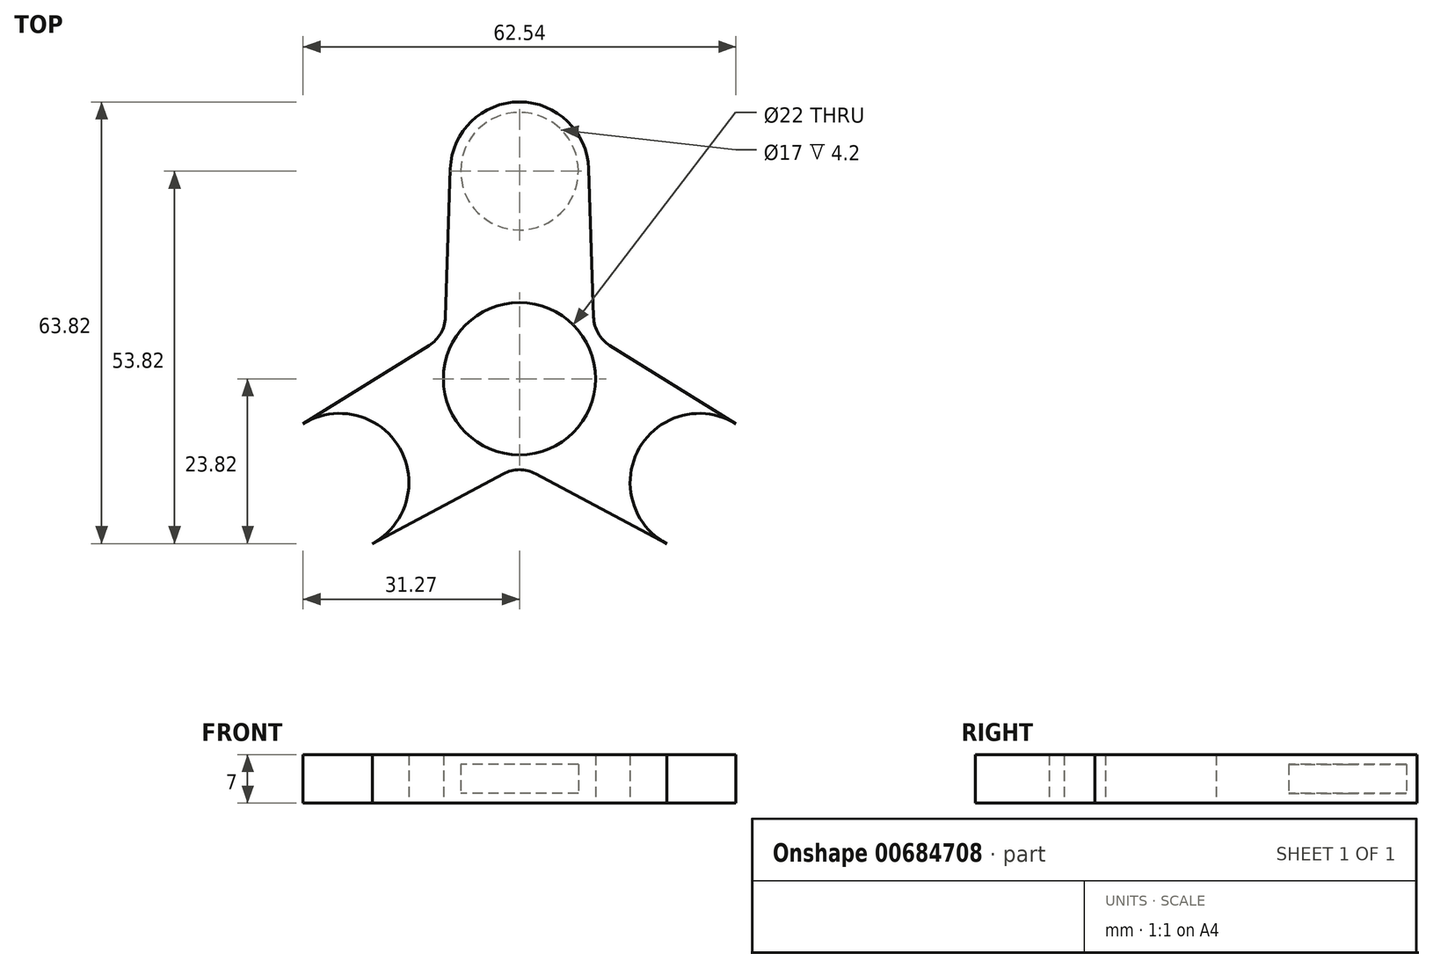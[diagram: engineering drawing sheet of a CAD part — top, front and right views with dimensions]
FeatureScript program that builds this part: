
annotation { "Feature Type Name" : "Feature", "Feature Type Description" : "" }
export const myFeature = defineFeature(function(context is Context, id is Id, definition is map)
    precondition{}
    {
        {
            var Q0;
            Q0=qCreatedBy(makeId("Top.planeOp"),FACE);
            var sketch = newSketch(context, id + "F0", { "sketchPlane" : qUnion([Q0])});
            skCircle(sketch, "E0", {"center": v(0, 0) * mm, "radius": 11 * mm});
            skLineSegment(sketch, "E1", {"start": v(-51.96, 30) * mm, "end": v(51.96, -30) * mm, "construction": true});
            skLineSegment(sketch, "E2.MirrorCS", {"start": v(51.96, 30) * mm, "end": v(-51.96, -30) * mm, "construction": true});
            skCircle(sketch, "E3", {"center": v(0, 30) * mm, "radius": 10 * mm});
            skCircle(sketch, "E4.MirrorC", {"center": v(-25.98, -15) * mm, "radius": 10 * mm});
            skCircle(sketch, "E5.MirrorC", {"center": v(25.98, -15) * mm, "radius": 10 * mm});
            skLineSegment(sketch, "E6", {"start": v(-10, 30.33) * mm, "end": v(-10.7, 8.9) * mm});
            skLineSegment(sketch, "E7", {"start": v(-13.06, 4.82) * mm, "end": v(-31.27, -6.51) * mm});
            skLineSegment(sketch, "E8", {"start": v(10, 30.33) * mm, "end": v(10.7, 8.9) * mm});
            skLineSegment(sketch, "E9.MirrorCS", {"start": v(-21.27, -23.82) * mm, "end": v(-2.35, -13.73) * mm});
            skLineSegment(sketch, "E10.MirrorCS", {"start": v(21.27, -23.82) * mm, "end": v(2.35, -13.73) * mm});
            skLineSegment(sketch, "E11.MirrorCS", {"start": v(31.27, -6.51) * mm, "end": v(13.06, 4.82) * mm});
            skPoint(sketch, "E12.newPointA", {"position": v(-11, 0) * mm});
            skArc(sketch, "E12.filletArc", {"start": v(-13.06, 4.82) * mm, "mid": v(-11.38, 6.57) * mm, "end": v(-10.7, 8.9) * mm});
            skPoint(sketch, "E13.newPointA", {"position": v(5.5, 9.53) * mm});
            skPoint(sketch, "E13.newPointB", {"position": v(11, 0) * mm});
            skArc(sketch, "E13.filletArc", {"start": v(10.7, 8.9) * mm, "mid": v(11.38, 6.57) * mm, "end": v(13.06, 4.82) * mm});
            skPoint(sketch, "E14.newPointA", {"position": v(5.5, -9.53) * mm});
            skPoint(sketch, "E14.newPointB", {"position": v(-5.5, -9.53) * mm});
            skArc(sketch, "E14.filletArc", {"start": v(2.35, -13.73) * mm, "mid": v(0, -13.14) * mm, "end": v(-2.35, -13.73) * mm});
            skSolve(sketch);
        }
        {
            var Q0;
            Q0=makeQuery(id+"F0.imprint","IMPRINT",FACE,{"disambiguationData":[TD([[makeQuery(id+"F0.imprint","IMPRINT",EDGE,{"derivedFrom":sQuery(id+"F0.wireOp",EDGE,"E0")}),-1.0]])]});
            var Q1;
            {var subQ0=sQuery(id+"F0.wireOp",EDGE,"E3");var subQ1=makeQuery(id+"F0.imprint","INTERSECT",VERTEX,{"derivedFrom":[subQ0,sQuery(id+"F0.wireOp",EDGE,"E8")]});Q1=makeQuery(id+"F0.imprint","IMPRINT",FACE,{"disambiguationData":[TD([[makeQuery(id+"F0.imprint","IMPRINT",EDGE,{"disambiguationData":[TD([[subQ1,-1.0]])],"derivedFrom":subQ0}),1.0]])]});}
            var Q2;
            {var subQ0=sQuery(id+"F0.wireOp",EDGE,"E4.MirrorC");var subQ1=makeQuery(id+"F0.imprint","INTERSECT",VERTEX,{"derivedFrom":[subQ0,sQuery(id+"F0.wireOp",EDGE,"E7")]});Q2=makeQuery(id+"F0.imprint","IMPRINT",FACE,{"disambiguationData":[TD([[makeQuery(id+"F0.imprint","IMPRINT",EDGE,{"disambiguationData":[TD([[subQ1,1.0]])],"derivedFrom":subQ0}),-1.0]])]});}
            var Q3;
            {var subQ0=sQuery(id+"F0.wireOp",EDGE,"E5.MirrorC");var subQ1=makeQuery(id+"F0.imprint","INTERSECT",VERTEX,{"derivedFrom":[subQ0,sQuery(id+"F0.wireOp",EDGE,"E11.MirrorCS")]});Q3=makeQuery(id+"F0.imprint","IMPRINT",FACE,{"disambiguationData":[TD([[makeQuery(id+"F0.imprint","IMPRINT",EDGE,{"disambiguationData":[TD([[subQ1,-1.0]])],"derivedFrom":subQ0}),-1.0]])]});}
            var Q4;
            {var subQ5=sQuery(id+"F0.wireOp",EDGE,"lwHCKfIK-zS6e-CTAC-9HsI-oUIeT1y9pyuL");Q4=makeQuery(id+"F0.imprint","IMPRINT",FACE,{"disambiguationData":[TD([[makeQuery(id+"F0.imprint","IMPRINT",EDGE,{"derivedFrom":subQ5}),1.0]])]});}
            var Q5;
            {var subQ1=sQuery(id+"F0.wireOp",EDGE,"E8");Q5=makeQuery(id+"F0.imprint","IMPRINT",FACE,{"disambiguationData":[TD([[makeQuery(id+"F0.imprint","IMPRINT",EDGE,{"derivedFrom":subQ1}),1.0]])]});}
            extrude(context, id + "F1", {"entities" : qUnion([Q0, Q1, Q2, Q3, Q4, Q5]), "depth" : 7 * mm, "offsetDistance" : 25 * mm});
        }
        {
            var Q0;
            Q0=qCreatedBy(makeId("Top.planeOp"),FACE);
            cPlane(context, id + "F2", {"entities" : qUnion([Q0]), "cplaneType" : CPlaneType.OFFSET, "offset" : 1.4 * mm, "width" : 150 * mm, "height" : 150 * mm});
        }
        {
            var Q0;
            Q0=qCreatedBy(id+"F2.planeOp",FACE);
            var sketch = newSketch(context, id + "F3", { "sketchPlane" : qUnion([Q0])});
            skPoint(sketch, "E15.0", {"position": v(0, 30) * mm});
            skPoint(sketch, "E16.0", {"position": v(25.98, -15) * mm});
            skPoint(sketch, "E17.0", {"position": v(-25.98, -15) * mm});
            skCircle(sketch, "E18", {"center": v(25.98, -15) * mm, "radius": 8.5 * mm});
            skCircle(sketch, "E19", {"center": v(-25.98, -15) * mm, "radius": 8.5 * mm});
            skCircle(sketch, "E20", {"center": v(0, 30) * mm, "radius": 8.5 * mm});
            skSolve(sketch);
        }
        {
            var Q0;
            Q0 = qSketchRegion(id + "F3", true);
            extrude(context, id + "F4", {"entities" : qUnion([Q0]), "operationType" : NewBodyOperationType.REMOVE, "depth" : 4.2 * mm, "offsetDistance" : 25 * mm});
        }
    });
